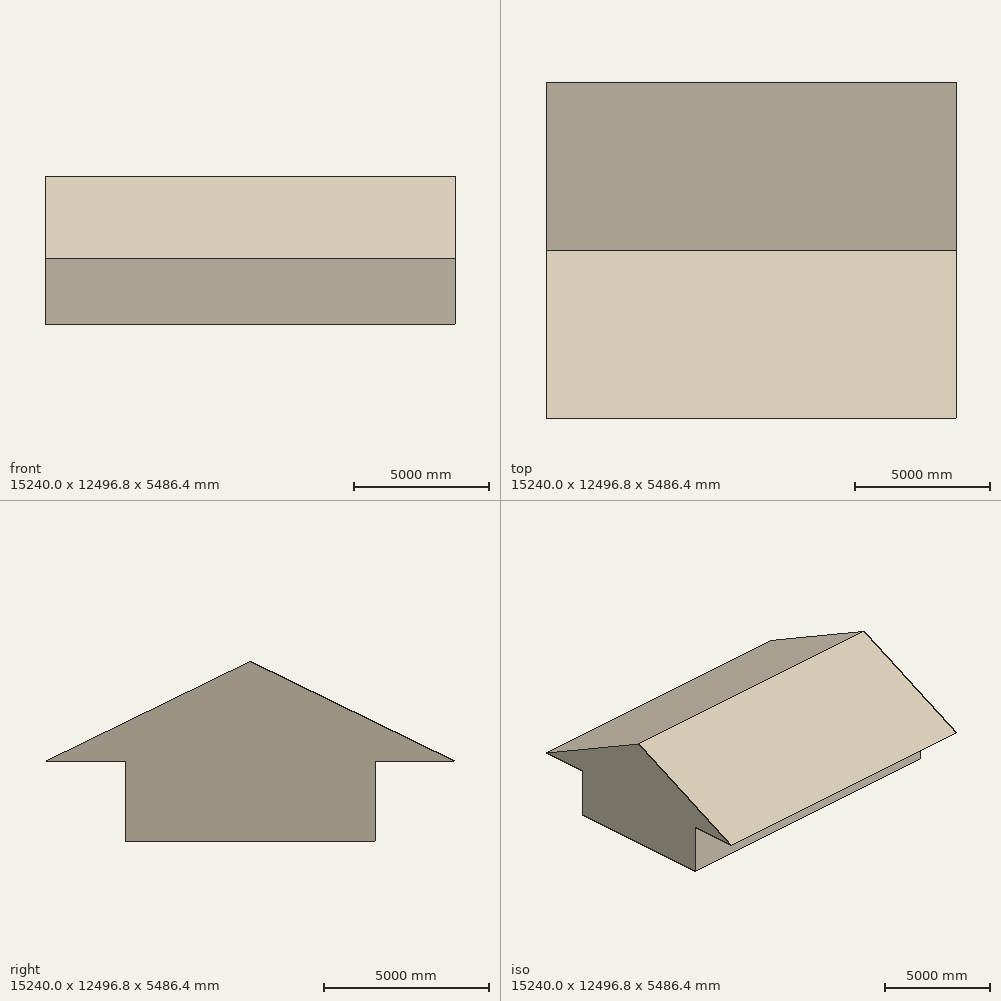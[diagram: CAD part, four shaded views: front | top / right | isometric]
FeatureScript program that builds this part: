
annotation { "Feature Type Name" : "Feature", "Feature Type Description" : "" }
export const myFeature = defineFeature(function(context is Context, id is Id, definition is map)
    precondition{}
    {
        {
            var Q0;
            Q0=qCreatedBy(makeId("Top.planeOp"),FACE);
            var sketch = newSketch(context, id + "F0", { "sketchPlane" : qUnion([Q0])});
            skLineSegment(sketch, "E0.bottom", {"start": v(-7619.88, 1786.58) * mm, "end": v(7620.12, 1786.58) * mm});
            skLineSegment(sketch, "E0.top", {"start": v(-7619.88, -5833.42) * mm, "end": v(7620.12, -5833.42) * mm});
            skLineSegment(sketch, "E0.left", {"start": v(-7619.88, 1786.58) * mm, "end": v(-7619.88, -5833.42) * mm});
            skLineSegment(sketch, "E0.right", {"start": v(7620.12, 1786.58) * mm, "end": v(7620.12, -5833.42) * mm});
            skSolve(sketch);
        }
        {
            var Q0;
            Q0=makeQuery(id+"F0.imprint","IMPRINT",FACE,{"disambiguationData":[TD([[makeQuery(id+"F0.imprint","IMPRINT",EDGE,{"derivedFrom":sQuery(id+"F0.wireOp",EDGE,"E0.bottom")}),-1.0]])]});
            extrude(context, id + "F1", {"entities" : qUnion([Q0]), "depth" : 2438.4 * mm, "offsetDistance" : 25.4 * mm});
        }
        {
            var Q0;
            Q0=makeQuery(id+"F1.opExtrude","SWEPT_FACE",FACE,{"disambiguationData":[OSD([sQuery(id+"F0.wireOp",EDGE,"E0.right")])]});
            var sketch = newSketch(context, id + "F2", { "sketchPlane" : qUnion([Q0])});
            skLineSegment(sketch, "E1", {"start": v(-8271.82, 2438.4) * mm, "end": v(-2023.42, 5486.4) * mm});
            skLineSegment(sketch, "E2", {"start": v(-2023.42, 5486.4) * mm, "end": v(4224.98, 2438.4) * mm});
            skLineSegment(sketch, "E3", {"start": v(4224.98, 2438.4) * mm, "end": v(-8271.82, 2438.4) * mm});
            skSolve(sketch);
        }
        {
            var Q0;
            {var subQ5=sQuery(id+"F2.wireOp",EDGE,"E1");Q0=makeQuery(id+"F2.imprint","IMPRINT",FACE,{"disambiguationData":[TD([[makeQuery(id+"F2.imprint","IMPRINT",EDGE,{"derivedFrom":subQ5}),-1.0]])]});}
            var Q1;
            Q1=makeQuery(id+"F1.opExtrude","SWEPT_FACE",FACE,{"disambiguationData":[OSD([sQuery(id+"F0.wireOp",EDGE,"E0.left")])]});
            extrude(context, id + "F3", {"entities" : qUnion([Q0]), "operationType" : NewBodyOperationType.ADD, "endBound" : BoundingType.UP_TO_SURFACE, "oppositeDirection" : true, "depth" : 25.4 * mm, "endBoundEntityFace" : qUnion([Q1]), "offsetDistance" : 25.4 * mm});
        }
    });
